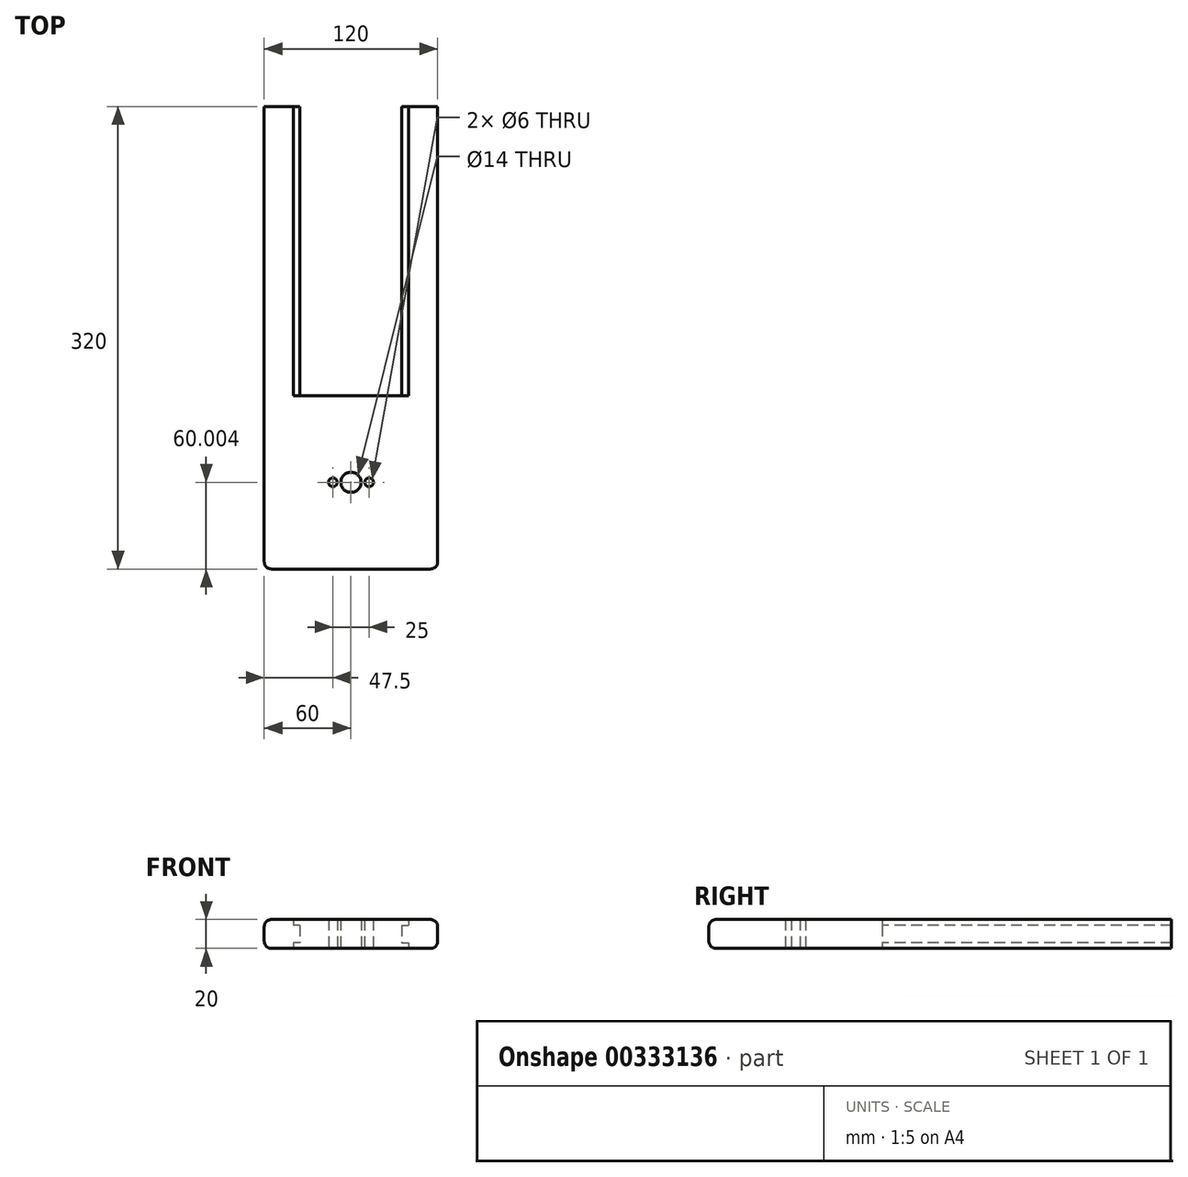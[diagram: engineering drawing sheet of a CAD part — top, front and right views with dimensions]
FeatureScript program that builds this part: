
annotation { "Feature Type Name" : "Feature", "Feature Type Description" : "" }
export const myFeature = defineFeature(function(context is Context, id is Id, definition is map)
    precondition{}
    {
        {
            var Q0;
            Q0=qCreatedBy(makeId("Top.planeOp"),FACE);
            var sketch = newSketch(context, id + "F0", { "sketchPlane" : qUnion([Q0])});
            skLineSegment(sketch, "E0.bottom", {"start": v(-60, 199.51) * mm, "end": v(60, 199.51) * mm});
            skLineSegment(sketch, "E0.top", {"start": v(-60, -120.49) * mm, "end": v(60, -120.49) * mm});
            skLineSegment(sketch, "E0.left", {"start": v(-60, 199.51) * mm, "end": v(-60, -120.49) * mm});
            skLineSegment(sketch, "E0.right", {"start": v(60, 199.51) * mm, "end": v(60, -120.49) * mm});
            skCircle(sketch, "E1", {"center": v(0, -60.49) * mm, "radius": 7 * mm});
            skCircle(sketch, "E2", {"center": v(-12.5, -60.49) * mm, "radius": 3 * mm});
            skCircle(sketch, "E3", {"center": v(12.5, -60.49) * mm, "radius": 3 * mm});
            skLineSegment(sketch, "E4.bottom", {"start": v(-40, 201.51) * mm, "end": v(40, 201.51) * mm});
            skLineSegment(sketch, "E4.top", {"start": v(-40, -0.49) * mm, "end": v(40, -0.49) * mm});
            skLineSegment(sketch, "E4.left", {"start": v(-40, 199.51) * mm, "end": v(-40, -0.49) * mm});
            skLineSegment(sketch, "E4.right", {"start": v(40, 199.51) * mm, "end": v(40, -0.49) * mm});
            skSolve(sketch);
        }
        {
            var Q0;
            Q0=makeQuery(id+"F0.imprint","IMPRINT",FACE,{"disambiguationData":[TD([[makeQuery(id+"F0.imprint","IMPRINT",EDGE,{"derivedFrom":sQuery(id+"F0.wireOp",EDGE,"E0.top")}),1.0]])]});
            extrude(context, id + "F1", {"entities" : qUnion([Q0]), "endBound" : BoundingType.SYMMETRIC, "depth" : 20 * mm});
        }
        {
            var Q0;
            Q0=makeQuery(id+"F1.opExtrude","SWEPT_FACE",FACE,{"disambiguationData":[OSD([sQuery(id+"F0.wireOp",EDGE,"E4.left")])]});
            var sketch = newSketch(context, id + "F2", { "sketchPlane" : qUnion([Q0])});
            skLineSegment(sketch, "E5.bottom", {"start": v(199.51, -6) * mm, "end": v(-0.49, -6) * mm});
            skLineSegment(sketch, "E5.top", {"start": v(199.51, 6) * mm, "end": v(-0.49, 6) * mm});
            skLineSegment(sketch, "E5.left", {"start": v(199.51, -6) * mm, "end": v(199.51, 6) * mm});
            skLineSegment(sketch, "E5.right", {"start": v(-0.49, -6) * mm, "end": v(-0.49, 6) * mm});
            skSolve(sketch);
        }
        {
            var Q0;
            Q0 = qSketchRegion(id + "F2", true);
            extrude(context, id + "F3", {"entities" : qUnion([Q0]), "operationType" : NewBodyOperationType.ADD, "depth" : 4.5 * mm});
        }
        {
            var Q0;
            Q0=makeQuery(id+"F1.opExtrude","SWEPT_FACE",FACE,{"disambiguationData":[OSD([sQuery(id+"F0.wireOp",EDGE,"E4.right")])]});
            var sketch = newSketch(context, id + "F4", { "sketchPlane" : qUnion([Q0])});
            skLineSegment(sketch, "E6.bottom", {"start": v(-199.51, -6) * mm, "end": v(0.49, -6) * mm});
            skLineSegment(sketch, "E6.top", {"start": v(-199.51, 6) * mm, "end": v(0.49, 6) * mm});
            skLineSegment(sketch, "E6.left", {"start": v(-199.51, -6) * mm, "end": v(-199.51, 6) * mm});
            skLineSegment(sketch, "E6.right", {"start": v(0.49, -6) * mm, "end": v(0.49, 6) * mm});
            skSolve(sketch);
        }
        {
            var Q0;
            Q0 = qSketchRegion(id + "F4", true);
            extrude(context, id + "F5", {"entities" : qUnion([Q0]), "operationType" : NewBodyOperationType.ADD, "depth" : 5 * mm});
        }
        {
            var Q0;
            Q0=makeQuery(id+"F1.opExtrude","CAP_EDGE",EDGE,{"disambiguationData":[OSD([sQuery(id+"F0.wireOp",EDGE,"E0.left")])],"isStart":false});
            fillet(context, id + "F6", {"entities" : qUnion([Q0]), "radius" : 5 * mm, "tangentPropagation" : true, "allowEdgeOverflow" : false});
        }
        {
            var Q0;
            Q0=makeQuery(id+"F1.opExtrude","CAP_EDGE",EDGE,{"disambiguationData":[OSD([sQuery(id+"F0.wireOp",EDGE,"E0.left")])],"isStart":true});
            fillet(context, id + "F7", {"entities" : qUnion([Q0]), "radius" : 5 * mm, "tangentPropagation" : true, "allowEdgeOverflow" : false});
        }
        {
            var Q0;
            Q0=makeQuery(id+"F1.opExtrude","CAP_EDGE",EDGE,{"disambiguationData":[OSD([sQuery(id+"F0.wireOp",EDGE,"E0.right")])],"isStart":true});
            fillet(context, id + "F8", {"entities" : qUnion([Q0]), "radius" : 5 * mm, "tangentPropagation" : true, "allowEdgeOverflow" : false});
        }
        {
            var Q0;
            Q0=makeQuery(id+"F1.opExtrude","CAP_EDGE",EDGE,{"disambiguationData":[OSD([sQuery(id+"F0.wireOp",EDGE,"E0.right")])],"isStart":false});
            fillet(context, id + "F9", {"entities" : qUnion([Q0]), "radius" : 5 * mm, "tangentPropagation" : true, "allowEdgeOverflow" : false});
        }
        {
            var Q0;
            Q0=makeQuery(id+"F1.opExtrude","CAP_EDGE",EDGE,{"disambiguationData":[OSD([sQuery(id+"F0.wireOp",EDGE,"E0.top")])],"isStart":false});
            fillet(context, id + "F10", {"entities" : qUnion([Q0]), "radius" : 5 * mm, "tangentPropagation" : true, "allowEdgeOverflow" : false});
        }
    });
